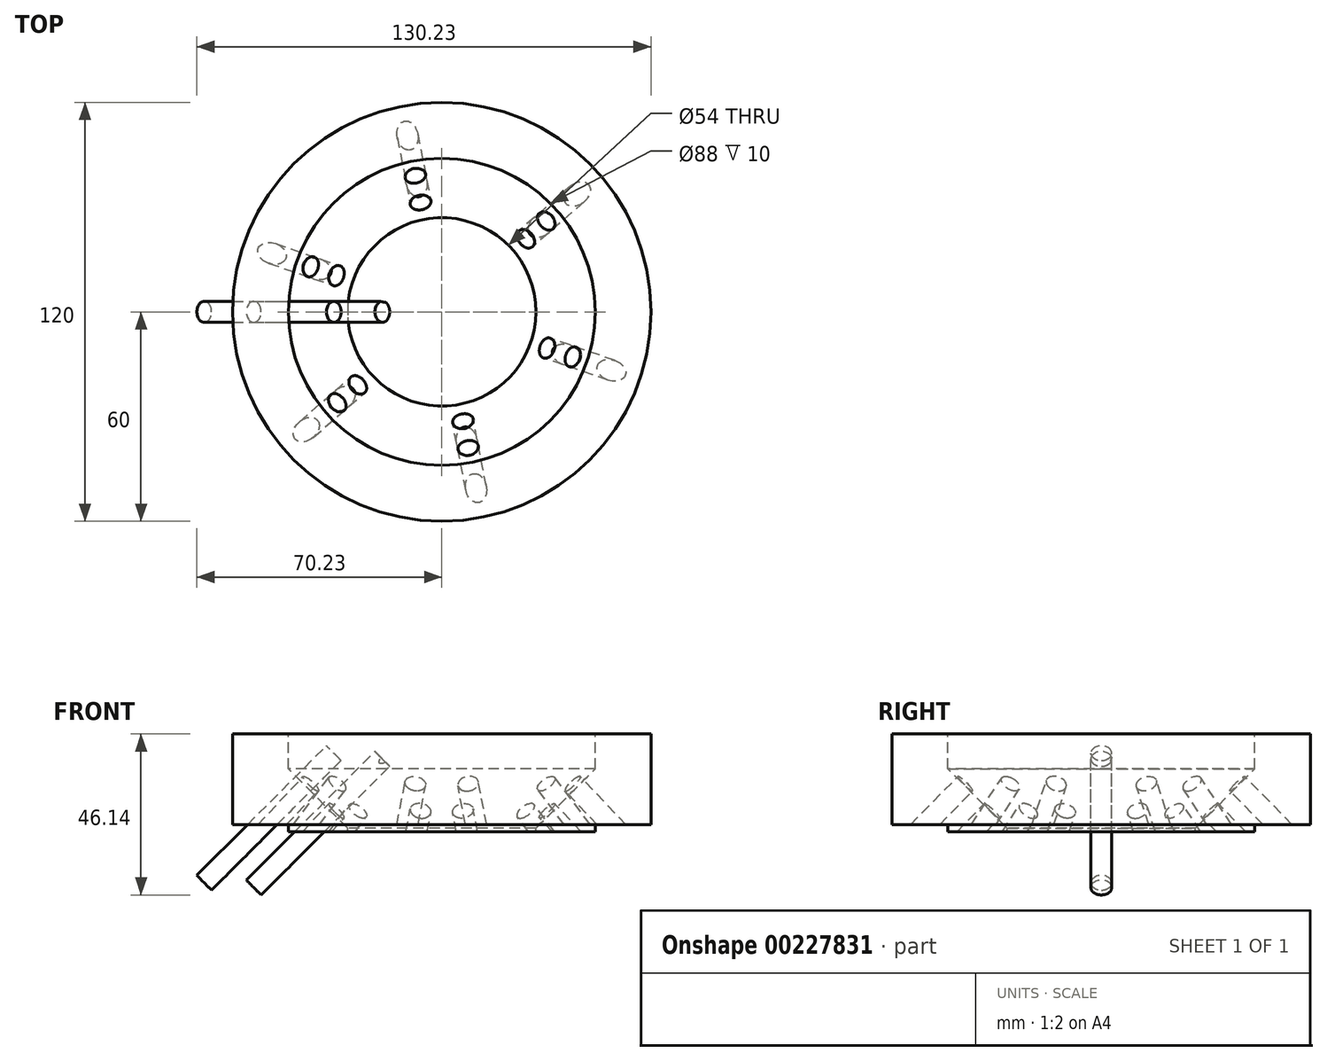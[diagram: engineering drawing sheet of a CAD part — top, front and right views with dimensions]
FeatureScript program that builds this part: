
annotation { "Feature Type Name" : "Feature", "Feature Type Description" : "" }
export const myFeature = defineFeature(function(context is Context, id is Id, definition is map)
    precondition{}
    {
        {
            var Q0;
            Q0=qCreatedBy(makeId("Front.planeOp"),FACE);
            var sketch = newSketch(context, id + "F0", { "sketchPlane" : qUnion([Q0])});
            skLineSegment(sketch, "E0", {"start": v(0, 70.12) * mm, "end": v(0, -51.14) * mm, "construction": true});
            skLineSegment(sketch, "E1", {"start": v(-40, -25.13) * mm, "end": v(-40, -82.12) * mm, "construction": true});
            skLineSegment(sketch, "E2", {"start": v(-33.5, -13) * mm, "end": v(-33.5, -83.09) * mm, "construction": true});
            skLineSegment(sketch, "E3", {"start": v(-55, -23.79) * mm, "end": v(-55, -71.7) * mm, "construction": true});
            skPoint(sketch, "E4", {"position": v(-45, -20) * mm});
            skLineSegment(sketch, "E5", {"start": v(-27, -2) * mm, "end": v(-44, 15) * mm});
            skLineSegment(sketch, "E6", {"start": v(-44, 20) * mm, "end": v(0, 20) * mm, "construction": true});
            skLineSegment(sketch, "E7.trimOffspring", {"start": v(-44, 15) * mm, "end": v(-44, 25) * mm});
            skLineSegment(sketch, "E8", {"start": v(0, 20) * mm, "end": v(0, -2) * mm});
            skLineSegment(sketch, "E9", {"start": v(-15, -3) * mm, "end": v(-15, -14) * mm});
            skLineSegment(sketch, "E10.trimOffspring", {"start": v(-44, 25) * mm, "end": v(-60, 25) * mm});
            skLineSegment(sketch, "E11", {"start": v(-27, -14) * mm, "end": v(-60, -14) * mm, "construction": true});
            skLineSegment(sketch, "E12", {"start": v(-44, -3) * mm, "end": v(-26, -3) * mm});
            skLineSegment(sketch, "E13", {"start": v(-60.56, -2) * mm, "end": v(-7.47, -2) * mm, "construction": true});
            skLineSegment(sketch, "E14", {"start": v(-32.2, -0.13) * mm, "end": v(-20.33, 11.74) * mm, "construction": true});
            skLineSegment(sketch, "E15", {"start": v(-37.48, 3.07) * mm, "end": v(-25.45, 15.1) * mm, "construction": true});
            skLineSegment(sketch, "E16", {"start": v(-39.45, 6.77) * mm, "end": v(-29.58, 16.63) * mm, "construction": true});
            skLineSegment(sketch, "E17", {"start": v(-44.65, 10.05) * mm, "end": v(-35.06, 19.64) * mm, "construction": true});
            skPoint(sketch, "E18", {"position": v(-27, -2) * mm});
            skLineSegment(sketch, "E19", {"start": v(-27, -2) * mm, "end": v(-16.61, 8.39) * mm, "construction": true});
            skLineSegment(sketch, "E20", {"start": v(-60, 25) * mm, "end": v(-60, -1) * mm});
            skLineSegment(sketch, "E21", {"start": v(-27, -2) * mm, "end": v(-27, -3) * mm});
            skLineSegment(sketch, "E22", {"start": v(-44, -1) * mm, "end": v(-44, -3) * mm});
            skLineSegment(sketch, "E23", {"start": v(-67.6, -1) * mm, "end": v(-41.15, -1) * mm});
            skSolve(sketch);
        }
        {
            var Q0;
            Q0=makeQuery(id+"F0.imprint","IMPRINT",FACE,{"disambiguationData":[TD([[makeQuery(id+"F0.imprint","IMPRINT",EDGE,{"derivedFrom":sQuery(id+"F0.wireOp",EDGE,"E5")}),1.0]])]});
            var Q1;
            Q1=sQuery(id+"F0.wireOp",EDGE,"E8");
            revolve(context, id + "F1", {"entities" : qUnion([Q0]), "axis" : qUnion([Q1]), "revolveType" : RevolveType.FULL});
        }
        {
            var Q0;
            Q0=qCreatedBy(makeId("Front.planeOp"),FACE);
            var sketch = newSketch(context, id + "F2", { "sketchPlane" : qUnion([Q0])});
            skLineSegment(sketch, "E24.0", {"start": v(-55, -23.79) * mm, "end": v(-55, -71.7) * mm, "construction": true});
            skLineSegment(sketch, "E25.0", {"start": v(-33.5, -13) * mm, "end": v(-33.5, -83.09) * mm, "construction": true});
            skLineSegment(sketch, "E26.0", {"start": v(-70.23, -15.54) * mm, "end": v(-33.09, 21.61) * mm});
            skLineSegment(sketch, "E27", {"start": v(-30.98, 19.5) * mm, "end": v(-68.12, -17.64) * mm});
            skLineSegment(sketch, "E28", {"start": v(-33.09, 21.61) * mm, "end": v(-30.98, 19.5) * mm});
            skLineSegment(sketch, "E29", {"start": v(-70.23, -15.54) * mm, "end": v(-68.12, -17.64) * mm});
            skSolve(sketch);
        }
        {
            var Q0;
            Q0 = qSketchRegion(id + "F2", true);
            var Q1;
            Q1=sQuery(id+"F2.wireOp",EDGE,"E27");
            revolve(context, id + "F3", {"entities" : qUnion([Q0]), "axis" : qUnion([Q1]), "revolveType" : RevolveType.FULL});
        }
        {
            var Q0;
            Q0=makeQuery(id+"F3.opRevolve","SWEPT_BODY",BODY,{"disambiguationData":[OSD([sQuery(id+"F2.wireOp",EDGE,"E26.0"),sQuery(id+"F2.wireOp",EDGE,"E27"),sQuery(id+"F2.wireOp",EDGE,"E28"),sQuery(id+"F2.wireOp",EDGE,"BTjxJDAI-CfnJ-hfkt-lCJ7-kgF73TjLmZTi")])]});
            var Q1;
            Q1=sQuery(id+"F0.wireOp",EDGE,"E0");
            circularPattern(context, id + "F4", {"entities" : qUnion([Q0]), "axis" : qUnion([Q1]), "angle" : 19 * degree, "instanceCount" : 2, "equalSpace" : true});
        }
        {
            var Q0;
            Q0=makeQuery(id+"F4.opPattern","COPY",BODY,{"derivedFrom":makeQuery(id+"F3.opRevolve","SWEPT_BODY",BODY,{"disambiguationData":[OSD([sQuery(id+"F2.wireOp",EDGE,"E26.0"),sQuery(id+"F2.wireOp",EDGE,"E27"),sQuery(id+"F2.wireOp",EDGE,"E28"),sQuery(id+"F2.wireOp",EDGE,"BTjxJDAI-CfnJ-hfkt-lCJ7-kgF73TjLmZTi")])]}),"instanceName":"1"});
            var Q1;
            Q1=sQuery(id+"F0.wireOp",EDGE,"E0");
            circularPattern(context, id + "F5", {"operationType" : NewBodyOperationType.REMOVE, "entities" : qUnion([Q0]), "axis" : qUnion([Q1]), "angle" : 360 * degree, "instanceCount" : 6, "equalSpace" : true});
        }
        {
            var Q0;
            Q0=qCreatedBy(makeId("Front.planeOp"),FACE);
            var sketch = newSketch(context, id + "F6", { "sketchPlane" : qUnion([Q0])});
            skLineSegment(sketch, "E30.0", {"start": v(-27, -2) * mm, "end": v(-44, 15) * mm, "construction": true});
            skLineSegment(sketch, "E31", {"start": v(-17.04, 17.86) * mm, "end": v(-53.98, -19.08) * mm});
            skLineSegment(sketch, "E32", {"start": v(-19.16, 19.98) * mm, "end": v(-17.04, 17.86) * mm});
            skLineSegment(sketch, "E33", {"start": v(-56.04, -16.9) * mm, "end": v(-53.92, -19.02) * mm});
            skLineSegment(sketch, "E34", {"start": v(-19.16, 19.98) * mm, "end": v(-56.04, -16.9) * mm});
            skSolve(sketch);
        }
        {
            var Q0;
            Q0 = qSketchRegion(id + "F6", true);
            var Q1;
            Q1=sQuery(id+"F6.wireOp",EDGE,"E30.0");
            var Q2;
            Q2=sQuery(id+"F6.wireOp",EDGE,"E31");
            revolve(context, id + "F7", {"entities" : qUnion([Q0]), "surfaceEntities" : qUnion([Q1]), "axis" : qUnion([Q2]), "revolveType" : RevolveType.FULL});
        }
        {
            var Q0;
            Q0=makeQuery(id+"F7.opRevolve","SWEPT_BODY",BODY,{"disambiguationData":[OSD([sQuery(id+"F6.wireOp",EDGE,"0296a30f-b775-46fb-957b-19e912f0fa4b.0"),sQuery(id+"F6.wireOp",EDGE,"E31"),sQuery(id+"F6.wireOp",EDGE,"E32"),sQuery(id+"F6.wireOp",EDGE,"E33")])]});
            var Q1;
            Q1=sQuery(id+"F0.wireOp",EDGE,"E0");
            circularPattern(context, id + "F8", {"entities" : qUnion([Q0]), "axis" : qUnion([Q1]), "angle" : 19 * degree, "instanceCount" : 2, "equalSpace" : true});
        }
        {
            var Q0;
            Q0=makeQuery(id+"F8.opPattern","COPY",BODY,{"derivedFrom":makeQuery(id+"F7.opRevolve","SWEPT_BODY",BODY,{"disambiguationData":[OSD([sQuery(id+"F6.wireOp",EDGE,"0296a30f-b775-46fb-957b-19e912f0fa4b.0"),sQuery(id+"F6.wireOp",EDGE,"E31"),sQuery(id+"F6.wireOp",EDGE,"E32"),sQuery(id+"F6.wireOp",EDGE,"E33")])]}),"instanceName":"1"});
            var Q1;
            Q1=makeQuery(id+"F1.opRevolve","SWEPT_FACE",FACE,{"disambiguationData":[OSD([sQuery(id+"F0.wireOp",EDGE,"E5")])]});
            circularPattern(context, id + "F9", {"operationType" : NewBodyOperationType.REMOVE, "entities" : qUnion([Q0]), "axis" : qUnion([Q1]), "angle" : 360 * degree, "instanceCount" : 6, "equalSpace" : true});
        }
    });
